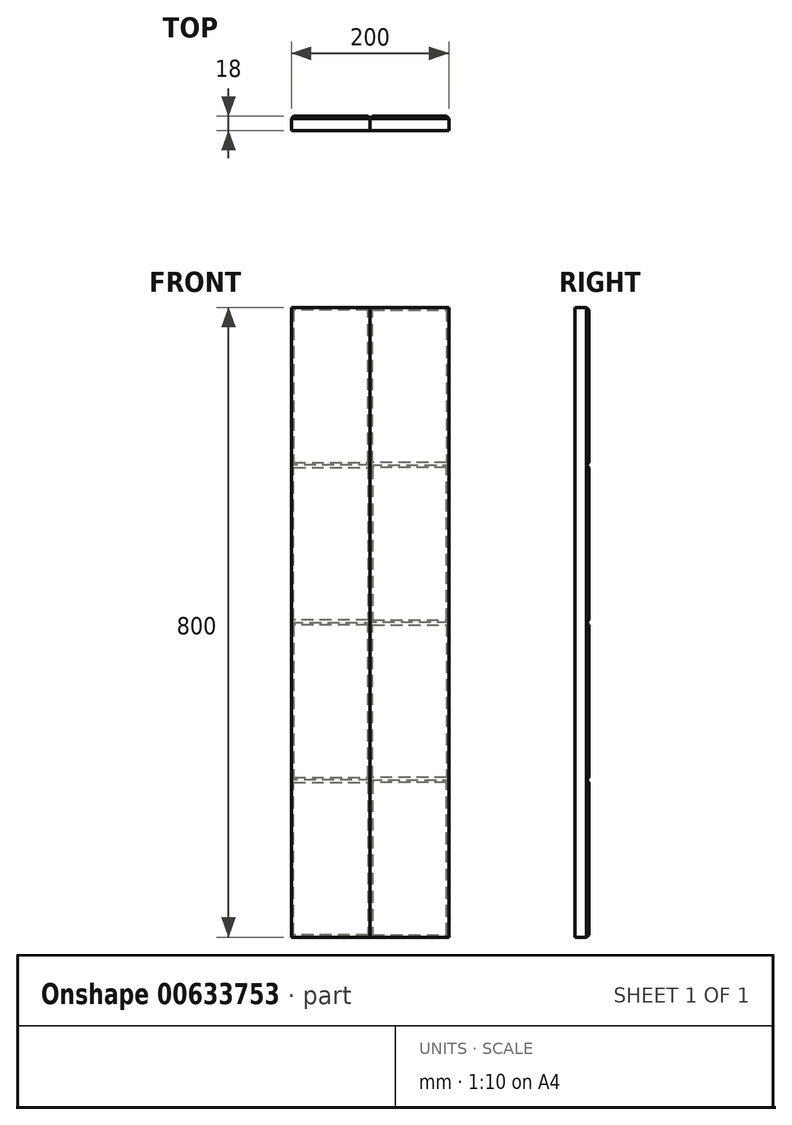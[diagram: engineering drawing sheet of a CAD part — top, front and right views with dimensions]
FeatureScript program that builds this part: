
annotation { "Feature Type Name" : "Feature", "Feature Type Description" : "" }
export const myFeature = defineFeature(function(context is Context, id is Id, definition is map)
    precondition{}
    {
        {
            var Q0;
            Q0=qCreatedBy(makeId("Right.planeOp"),FACE);
            var sketch = newSketch(context, id + "F0", { "sketchPlane" : qUnion([Q0])});
            skLineSegment(sketch, "E0.bottom", {"start": v(-40.85, 175.4) * mm, "end": v(-22.85, 175.4) * mm});
            skLineSegment(sketch, "E0.top", {"start": v(-40.85, -24.6) * mm, "end": v(-22.85, -24.6) * mm});
            skLineSegment(sketch, "E0.left", {"start": v(-40.85, 175.4) * mm, "end": v(-40.85, -24.6) * mm});
            skLineSegment(sketch, "E0.right", {"start": v(-22.85, 175.4) * mm, "end": v(-22.85, -24.6) * mm});
            skSolve(sketch);
        }
        {
            var Q0;
            Q0 = qSketchRegion(id + "F0", true);
            extrude(context, id + "F1", {"entities" : qUnion([Q0]), "depth" : 100 * mm, "offsetDistance" : 25 * mm});
        }
        {
            var Q0;
            Q0=makeQuery(id+"F1.opExtrude","SWEPT_EDGE",EDGE,{"disambiguationData":[OSD([sQuery(id+"F0.wireOp",EDGE,"E0.bottom"),sQuery(id+"F0.wireOp",EDGE,"E0.right")])]});
            var Q1;
            Q1=makeQuery(id+"F1.opExtrude","CAP_EDGE",EDGE,{"disambiguationData":[OSD([sQuery(id+"F0.wireOp",EDGE,"E0.right")])],"isStart":false});
            var Q2;
            Q2=makeQuery(id+"F1.opExtrude","CAP_EDGE",EDGE,{"disambiguationData":[OSD([sQuery(id+"F0.wireOp",EDGE,"E0.right")])],"isStart":true});
            var Q3;
            Q3=makeQuery(id+"F1.opExtrude","SWEPT_EDGE",EDGE,{"disambiguationData":[OSD([sQuery(id+"F0.wireOp",EDGE,"E0.top"),sQuery(id+"F0.wireOp",EDGE,"E0.right")])]});
            chamfer(context, id + "F2", {"entities" : qUnion([Q0, Q1, Q2, Q3]), "width" : 3 * mm, "tangentPropagation" : true});
        }
        {
            var Q0;
            Q0=makeQuery(id+"F1.opExtrude","SWEPT_BODY",BODY,{"disambiguationData":[OSD([sQuery(id+"F0.wireOp",EDGE,"E0.bottom"),sQuery(id+"F0.wireOp",EDGE,"E0.top"),sQuery(id+"F0.wireOp",EDGE,"E0.left"),sQuery(id+"F0.wireOp",EDGE,"E0.right")])]});
            var Q1;
            Q1=makeQuery(id+"F1.opExtrude","SWEPT_FACE",FACE,{"disambiguationData":[OSD([sQuery(id+"F0.wireOp",EDGE,"E0.bottom")])]});
            mirror(context, id + "F3", {"operationType" : NewBodyOperationType.ADD, "entities" : qUnion([Q0]), "mirrorPlane" : qUnion([Q1])});
        }
        {
            var Q0;
            Q0=makeQuery(id+"F1.opExtrude","SWEPT_BODY",BODY,{"disambiguationData":[OSD([sQuery(id+"F0.wireOp",EDGE,"E0.bottom"),sQuery(id+"F0.wireOp",EDGE,"E0.top"),sQuery(id+"F0.wireOp",EDGE,"E0.left"),sQuery(id+"F0.wireOp",EDGE,"E0.right")])]});
            var Q1;
            Q1=makeQuery(id+"F3.opPattern","COPY",FACE,{"derivedFrom":makeQuery(id+"F1.opExtrude","SWEPT_FACE",FACE,{"disambiguationData":[OSD([sQuery(id+"F0.wireOp",EDGE,"E0.top")])]}),"instanceName":"1"});
            mirror(context, id + "F4", {"operationType" : NewBodyOperationType.ADD, "entities" : qUnion([Q0]), "mirrorPlane" : qUnion([Q1])});
        }
        {
            var Q0;
            Q0=makeQuery(id+"F1.opExtrude","SWEPT_BODY",BODY,{"disambiguationData":[OSD([sQuery(id+"F0.wireOp",EDGE,"E0.bottom"),sQuery(id+"F0.wireOp",EDGE,"E0.top"),sQuery(id+"F0.wireOp",EDGE,"E0.left"),sQuery(id+"F0.wireOp",EDGE,"E0.right")])]});
            var Q1;
            {var subQ0=makeQuery(id+"F1.opExtrude","CAP_FACE",FACE,{"disambiguationData":[OSD([sQuery(id+"F0.wireOp",EDGE,"E0.bottom"),sQuery(id+"F0.wireOp",EDGE,"E0.top"),sQuery(id+"F0.wireOp",EDGE,"E0.left"),sQuery(id+"F0.wireOp",EDGE,"E0.right")])],"isStart":false});var subQ1=makeQuery(id+"F3.boolean.opBoolean","MERGE",FACE,{"derivedFrom":[subQ0,makeQuery(id+"F3.opPattern","COPY",FACE,{"derivedFrom":subQ0,"instanceName":"1"})]});Q1=makeQuery(id+"F4.boolean.opBoolean","MERGE",FACE,{"derivedFrom":[subQ1,makeQuery(id+"F4.opPattern","COPY",FACE,{"derivedFrom":subQ1,"instanceName":"1"})]});}
            mirror(context, id + "F5", {"entities" : qUnion([Q0]), "mirrorPlane" : qUnion([Q1])});
        }
    });
